# Revit family: Maxlogic Firefighter's portable telephone station for 4 units (excluding phones)
name_source: partatom
category: Fire Alarm Devices
units: mm (PartAtom-declared; Revit-internal decimal feet)

## family parameters
Cut with Voids When Loaded = No
Host = Face
Maintain Annotation Orientation = Yes
OmniClass Number = 23.85.30.21
OmniClass Title = Environmental Detection/Registration
Part Type = Normal
Room Calculation Point = No
Round Connector Dimension = Use Diameter
Shared = No

## types (1)
- Maxlogic Firefighter's portable telephone station for 4 units (excluding phones)
    Color = Red
    Cost = 0 $
    Default Elevation = 0 mm  [stored 0 ft]
    Description = Firefighter's portable telephone station for 4 units (excluding phones)
    Fax Number = (+)90 216 466 45 10
    Firefighter's portable telephone = ML-5013
    Installation Manual = https://mavilielektronik.com
    Main Material = Metal Red
    Manufacturer = Mavili Elektronik Ticaret A.Ş.
    Model = Maxlogic
    Mounting surface = Wall mounting
    Nominal Depth = 111 mm
    Nominal Height = 300 mm
    Nominal Width = 400 mm
    Operating temperature = (-10°C) - (+55°C)
    Product Code = ML-5014
    Secondary Material = Metal Grey
    URL = https://www.mavili.com.tr
    Warranty Duration Labor = 2
    Warranty Duration Parts = 2
    Warranty Duration Unit = Year

note: [stored X ft] marks values corroborated as IEEE doubles in the binary element streams (Revit-internal decimal feet)

## geometry (parser evidence)
native form markers: Sweep x1
no freeform markers — native parametric forms only
